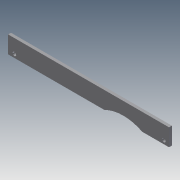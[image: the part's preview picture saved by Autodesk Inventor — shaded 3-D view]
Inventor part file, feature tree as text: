
AUTODESK INVENTOR PART (.ipt)
format: ipt  version: 2011 (Build 150239000, 239)  size: 132,608 bytes
history: native  units: in
note: dims shown in document units (in); Inventor stores cm internally (conversion verified against a paired STEP export)
features: extrude x9, sketch x9
ambient origin geometry x8: Origin, YZ Plane, XZ Plane, XY Plane, X Axis, Y Axis, Z Axis, Center Point
bodies: Solid1 (feature_tree)
feature tree (18):
  extrude  "Extrusion1"  Depth=0.5in
  extrude  "Extrusion2"  Depth=6.735in
  extrude  "Extrusion3"  Depth=0.156in
  extrude  "Extrusion4"  Depth=0.25in TaperAngle=0.0deg
  extrude  "Extrusion5"  Depth=0.15in
  extrude  "Extrusion6"  Depth=0.156in
  extrude  "Extrusion7"  Depth=0.25in TaperAngle=0.0deg
  extrude  "Extrusion8"  Depth=0.1in TaperAngle=0.0deg
  extrude  "Extrusion9"  Depth=0.125in TaperAngle=0.0deg
  sketch  "Sketch1"  dims[d0=7.25in d1=0.5in]
  sketch  "Sketch2"  dims[d2=3.3675in d3=6.735in]
  sketch  "Sketch3"  dims[d4=0.1in d5=0.156in]
  sketch  "Sketch4"  dims[d6=0.125in d7=0.0in d8=0.25in d9=0.0in]
  sketch  "Sketch5"  dims[d10=0.25in d11=0.0in d12=0.15in]
  sketch  "Sketch6"  dims[d13=3.25in d14=0.156in]
  sketch  "Sketch7"  dims[d15=6.5in d16=0.25in d17=0.0in]
  sketch  "Sketch8"  dims[d18=0.15in d19=0.0in d20=0.1in d21=0.0in]
  sketch  "Sketch9"  dims[d22=0.125in d23=0.0in d24=0.125in d25=0.0in d26=1.765in d27=1.765in d28=3.625in d29=1.0in d30=0.0in]
